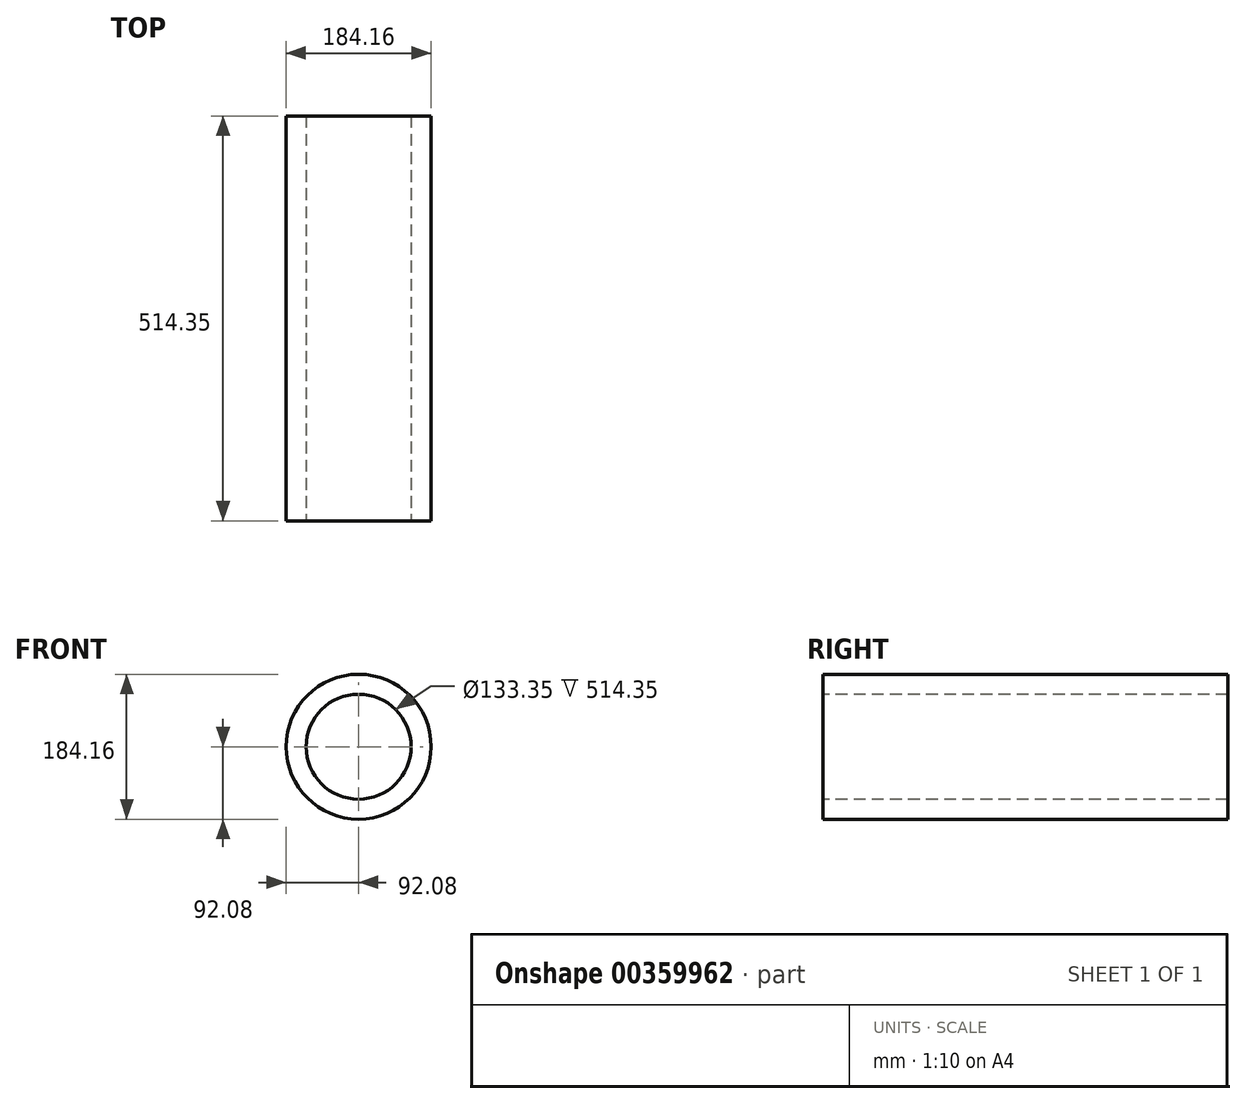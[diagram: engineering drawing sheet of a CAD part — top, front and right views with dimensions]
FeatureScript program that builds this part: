
annotation { "Feature Type Name" : "Feature", "Feature Type Description" : "" }
export const myFeature = defineFeature(function(context is Context, id is Id, definition is map)
    precondition{}
    {
        {
            var Q0;
            Q0=qCreatedBy(makeId("Front.planeOp"),FACE);
            var sketch = newSketch(context, id + "F0", { "sketchPlane" : qUnion([Q0])});
            skCircle(sketch, "E0", {"center": v(0, 0) * mm, "radius": 92.08 * mm});
            skCircle(sketch, "E1", {"center": v(0, 0) * mm, "radius": 66.68 * mm});
            skSolve(sketch);
        }
        {
            var Q0;
            Q0=makeQuery(id+"F0.imprint","IMPRINT",FACE,{"disambiguationData":[TD([[makeQuery(id+"F0.imprint","IMPRINT",EDGE,{"derivedFrom":sQuery(id+"F0.wireOp",EDGE,"E0")}),1.0]])]});
            extrude(context, id + "F1", {"entities" : qUnion([Q0]), "oppositeDirection" : true, "depth" : 514.35 * mm});
        }
    });
